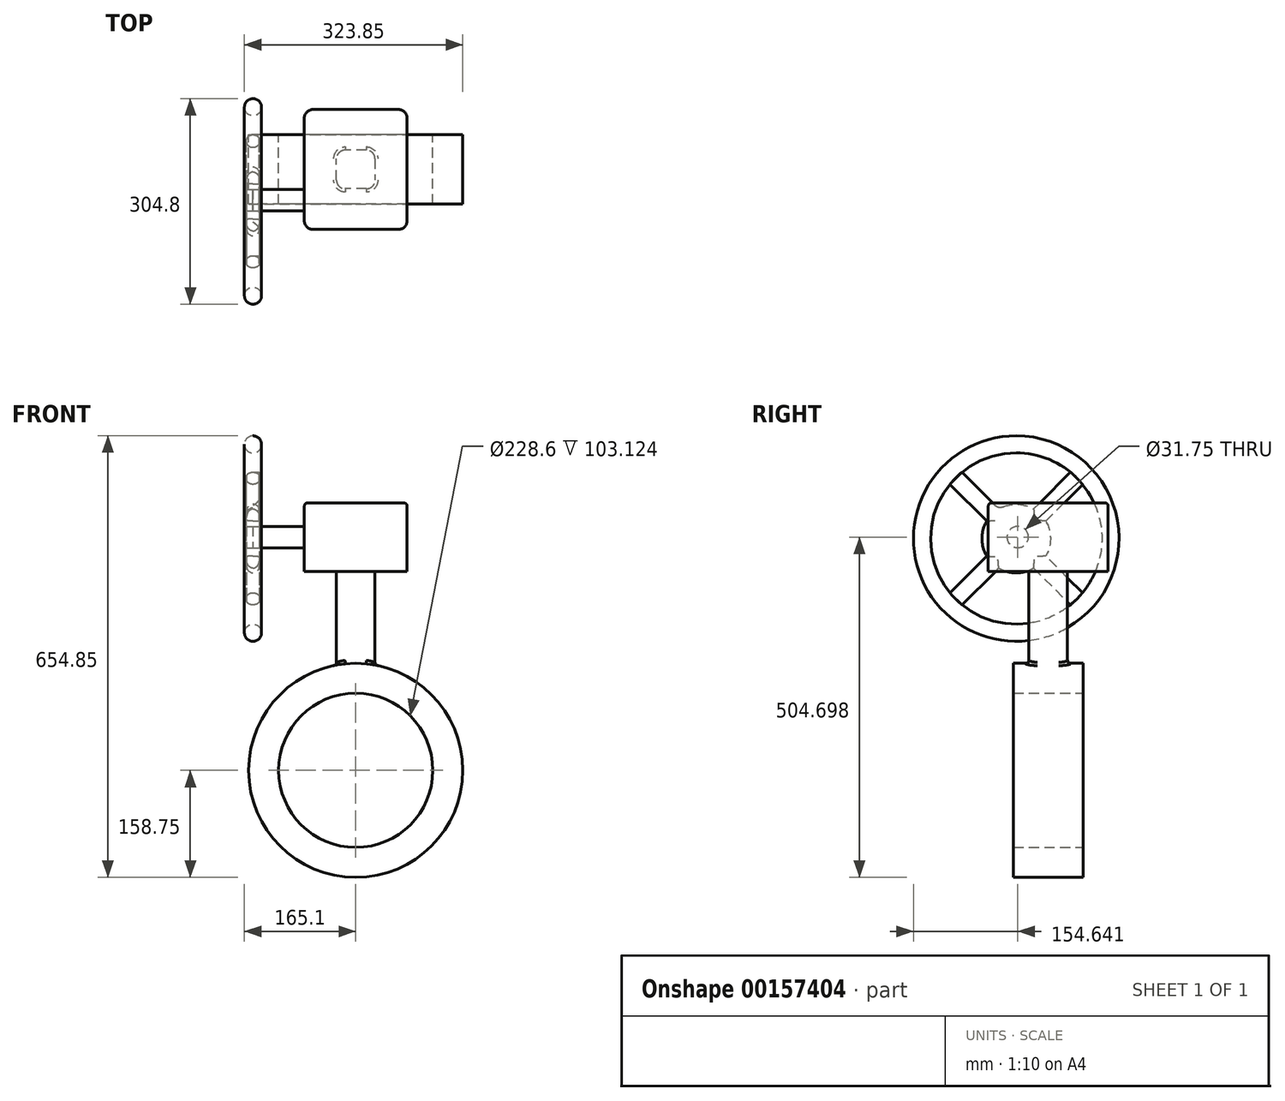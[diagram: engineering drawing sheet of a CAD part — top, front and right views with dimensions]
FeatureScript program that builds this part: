
annotation { "Feature Type Name" : "Feature", "Feature Type Description" : "" }
export const myFeature = defineFeature(function(context is Context, id is Id, definition is map)
    precondition{}
    {
        {
            var Q0;
            Q0=qCreatedBy(makeId("Front.planeOp"),FACE);
            var sketch = newSketch(context, id + "F0", { "sketchPlane" : qUnion([Q0])});
            skCircle(sketch, "E0", {"center": v(0, 0) * mm, "radius": 158.75 * mm});
            skSolve(sketch);
        }
        {
            var Q0;
            Q0=makeQuery(id+"F0.imprint","IMPRINT",FACE,{"disambiguationData":[TD([[makeQuery(id+"F0.imprint","IMPRINT",EDGE,{"derivedFrom":sQuery(id+"F0.wireOp",EDGE,"E0")}),1.0]])]});
            extrude(context, id + "F1", {"entities" : qUnion([Q0]), "depth" : 103.12 * mm, "symmetric" : true});
        }
        {
            var Q0;
            Q0=qCreatedBy(makeId("Top.planeOp"),FACE);
            cPlane(context, id + "F2", {"entities" : qUnion([Q0]), "cplaneType" : CPlaneType.OFFSET, "offset" : 152.4 * mm, "width" : 152.4 * mm, "height" : 152.4 * mm});
        }
        {
            var Q0;
            Q0=qCreatedBy(id+"F2.planeOp",FACE);
            var sketch = newSketch(context, id + "F3", { "sketchPlane" : qUnion([Q0])});
            skLineSegment(sketch, "E1.bottom", {"start": v(28.57, -28.58) * mm, "end": v(-28.58, -28.58) * mm});
            skLineSegment(sketch, "E1.top", {"start": v(28.57, 28.58) * mm, "end": v(-28.58, 28.57) * mm});
            skLineSegment(sketch, "E1.left", {"start": v(28.57, -28.57) * mm, "end": v(28.57, 28.58) * mm});
            skLineSegment(sketch, "E1.right", {"start": v(-28.58, -28.58) * mm, "end": v(-28.58, 28.57) * mm});
            skPoint(sketch, "E1.middle", {"position": v(0, 0) * mm});
            skSolve(sketch);
        }
        {
            var Q0;
            Q0 = qSketchRegion(id + "F3", true);
            extrude(context, id + "F4", {"entities" : qUnion([Q0]), "operationType" : NewBodyOperationType.ADD, "depth" : 142.75 * mm});
        }
        {
            var Q0;
            Q0=makeQuery(id+"F4.opExtrude","CAP_FACE",FACE,{"disambiguationData":[OSD([sQuery(id+"F3.wireOp",EDGE,"E1.bottom"),sQuery(id+"F3.wireOp",EDGE,"E1.top"),sQuery(id+"F3.wireOp",EDGE,"E1.left"),sQuery(id+"F3.wireOp",EDGE,"E1.right")])],"isStart":false});
            var sketch = newSketch(context, id + "F5", { "sketchPlane" : qUnion([Q0])});
            skLineSegment(sketch, "E2.bottom", {"start": v(76.2, -88.9) * mm, "end": v(-76.2, -88.9) * mm});
            skLineSegment(sketch, "E2.top", {"start": v(76.2, 88.9) * mm, "end": v(-76.2, 88.9) * mm});
            skLineSegment(sketch, "E2.left", {"start": v(76.2, -88.9) * mm, "end": v(76.2, 88.9) * mm});
            skLineSegment(sketch, "E2.right", {"start": v(-76.2, -88.9) * mm, "end": v(-76.2, 88.9) * mm});
            skPoint(sketch, "E2.middle", {"position": v(0, 0) * mm});
            skSolve(sketch);
        }
        {
            var Q0;
            Q0 = qSketchRegion(id + "F5", true);
            extrude(context, id + "F6", {"entities" : qUnion([Q0]), "operationType" : NewBodyOperationType.ADD, "depth" : 101.6 * mm});
        }
        {
            var Q0;
            Q0=makeQuery(id+"F6.opExtrude","SWEPT_FACE",FACE,{"disambiguationData":[OSD([sQuery(id+"F5.wireOp",EDGE,"E2.right")])]});
            var sketch = newSketch(context, id + "F7", { "sketchPlane" : qUnion([Q0])});
            skCircle(sketch, "E3", {"center": v(45.22, 345.95) * mm, "radius": 15.88 * mm});
            skPoint(sketch, "E3.centerSnap0", {"position": v(88.9, 345.95) * mm});
            skSolve(sketch);
        }
        {
            var Q0;
            Q0 = qSketchRegion(id + "F7", true);
            extrude(context, id + "F8", {"entities" : qUnion([Q0]), "operationType" : NewBodyOperationType.ADD, "depth" : 76.2 * mm});
        }
        {
            var Q0;
            Q0=makeQuery(id+"F8.opExtrude","CAP_FACE",FACE,{"disambiguationData":[OSD([sQuery(id+"F7.wireOp",EDGE,"E3")])],"isStart":false});
            var sketch = newSketch(context, id + "F9", { "sketchPlane" : qUnion([Q0])});
            skCircle(sketch, "E4", {"center": v(47.46, 343.7) * mm, "radius": 152.4 * mm});
            skArc(sketch, "E5", {"start": v(73.26, 387.46) * mm, "mid": v(47.46, 394.5) * mm, "end": v(21.66, 387.46) * mm});
            skCircle(sketch, "E6", {"center": v(47.46, 343.7) * mm, "radius": 127 * mm});
            skLineSegment(sketch, "E7.trimOffspring", {"start": v(91.22, 317.9) * mm, "end": v(145.8, 263.33) * mm});
            skLineSegment(sketch, "E8.trimOffspring", {"start": v(73.26, 299.94) * mm, "end": v(127.84, 245.37) * mm});
            skLineSegment(sketch, "E9.trimOffspring", {"start": v(21.66, 299.94) * mm, "end": v(-32.9, 245.37) * mm});
            skLineSegment(sketch, "E10.trimOffspring", {"start": v(3.7, 317.9) * mm, "end": v(-50.87, 263.33) * mm});
            skLineSegment(sketch, "E11.trimOffspring", {"start": v(3.7, 369.5) * mm, "end": v(-50.87, 424.08) * mm});
            skLineSegment(sketch, "E12.trimOffspring", {"start": v(21.66, 387.46) * mm, "end": v(-32.9, 442.04) * mm});
            skLineSegment(sketch, "E13.trimOffspring", {"start": v(73.26, 387.46) * mm, "end": v(127.84, 442.04) * mm});
            skLineSegment(sketch, "E14.trimOffspring", {"start": v(91.22, 369.5) * mm, "end": v(145.8, 424.08) * mm});
            skArc(sketch, "E15.trimOffspring", {"start": v(91.22, 317.9) * mm, "mid": v(98.26, 343.7) * mm, "end": v(91.22, 369.5) * mm});
            skArc(sketch, "E16.trimOffspring", {"start": v(21.66, 299.94) * mm, "mid": v(47.46, 292.9) * mm, "end": v(73.26, 299.94) * mm});
            skArc(sketch, "E17.trimOffspring", {"start": v(3.7, 369.5) * mm, "mid": v(-3.34, 343.7) * mm, "end": v(3.7, 317.9) * mm});
            skSolve(sketch);
        }
        {
            var Q0;
            Q0 = qSketchRegion(id + "F9", true);
            extrude(context, id + "F10", {"entities" : qUnion([Q0]), "depth" : 25.4 * mm, "symmetric" : true});
        }
        {
            var Q0;
            Q0=makeQuery(id+"F9.imprint","IMPRINT",FACE,{"disambiguationData":[TD([[makeQuery(id+"F9.imprint","IMPRINT",EDGE,{"derivedFrom":sQuery(id+"F9.wireOp",EDGE,"E5")}),1.0]])]});
            extrude(context, id + "F11", {"entities" : qUnion([Q0]), "depth" : 19.05 * mm, "symmetric" : true});
        }
        {
            var Q0;
            Q0=makeQuery(id+"F10.opExtrude","CAP_EDGE",EDGE,{"disambiguationData":[OSD([sQuery(id+"F9.wireOp",EDGE,"E6")])],"isStart":false});
            var Q1;
            Q1=makeQuery(id+"F10.opExtrude","CAP_EDGE",EDGE,{"disambiguationData":[OSD([sQuery(id+"F9.wireOp",EDGE,"E4")])],"isStart":false});
            var Q2;
            Q2=makeQuery(id+"F10.opExtrude","CAP_EDGE",EDGE,{"disambiguationData":[OSD([sQuery(id+"F9.wireOp",EDGE,"E4")])],"isStart":true});
            var Q3;
            Q3=makeQuery(id+"F10.opExtrude","CAP_EDGE",EDGE,{"disambiguationData":[OSD([sQuery(id+"F9.wireOp",EDGE,"E6")])],"isStart":true});
            fillet(context, id + "F12", {"entities" : qUnion([Q0, Q1, Q2, Q3]), "radius" : 12.7 * mm, "tangentPropagation" : true, "allowEdgeOverflow" : false});
        }
        {
            var Q0;
            Q0=makeQuery(id+"F11.opExtrude","CAP_EDGE",EDGE,{"disambiguationData":[OSD([sQuery(id+"F9.wireOp",EDGE,"E12.trimOffspring")])],"isStart":false});
            var Q1;
            Q1=makeQuery(id+"F11.opExtrude","CAP_EDGE",EDGE,{"disambiguationData":[OSD([sQuery(id+"F9.wireOp",EDGE,"E5")])],"isStart":false});
            var Q2;
            Q2=makeQuery(id+"F11.opExtrude","CAP_EDGE",EDGE,{"disambiguationData":[OSD([sQuery(id+"F9.wireOp",EDGE,"E13.trimOffspring")])],"isStart":false});
            var Q3;
            Q3=makeQuery(id+"F11.opExtrude","CAP_EDGE",EDGE,{"disambiguationData":[OSD([sQuery(id+"F9.wireOp",EDGE,"E11.trimOffspring")])],"isStart":false});
            var Q4;
            Q4=makeQuery(id+"F11.opExtrude","CAP_EDGE",EDGE,{"disambiguationData":[OSD([sQuery(id+"F9.wireOp",EDGE,"E17.trimOffspring")])],"isStart":false});
            var Q5;
            Q5=makeQuery(id+"F11.opExtrude","CAP_EDGE",EDGE,{"disambiguationData":[OSD([sQuery(id+"F9.wireOp",EDGE,"E10.trimOffspring")])],"isStart":false});
            var Q6;
            Q6=makeQuery(id+"F11.opExtrude","CAP_EDGE",EDGE,{"disambiguationData":[OSD([sQuery(id+"F9.wireOp",EDGE,"E14.trimOffspring")])],"isStart":false});
            var Q7;
            Q7=makeQuery(id+"F11.opExtrude","CAP_EDGE",EDGE,{"disambiguationData":[OSD([sQuery(id+"F9.wireOp",EDGE,"E15.trimOffspring")])],"isStart":false});
            var Q8;
            Q8=makeQuery(id+"F11.opExtrude","CAP_EDGE",EDGE,{"disambiguationData":[OSD([sQuery(id+"F9.wireOp",EDGE,"E7.trimOffspring")])],"isStart":false});
            var Q9;
            Q9=makeQuery(id+"F11.opExtrude","CAP_EDGE",EDGE,{"disambiguationData":[OSD([sQuery(id+"F9.wireOp",EDGE,"E8.trimOffspring")])],"isStart":false});
            var Q10;
            Q10=makeQuery(id+"F11.opExtrude","CAP_EDGE",EDGE,{"disambiguationData":[OSD([sQuery(id+"F9.wireOp",EDGE,"E16.trimOffspring")])],"isStart":false});
            var Q11;
            Q11=makeQuery(id+"F11.opExtrude","CAP_EDGE",EDGE,{"disambiguationData":[OSD([sQuery(id+"F9.wireOp",EDGE,"E9.trimOffspring")])],"isStart":false});
            var Q12;
            Q12=makeQuery(id+"F11.opExtrude","CAP_EDGE",EDGE,{"disambiguationData":[OSD([sQuery(id+"F9.wireOp",EDGE,"E14.trimOffspring")])],"isStart":true});
            var Q13;
            Q13=makeQuery(id+"F11.opExtrude","SWEPT_EDGE",EDGE,{"disambiguationData":[OSD([sQuery(id+"F9.wireOp",EDGE,"E5"),sQuery(id+"F9.wireOp",EDGE,"E13.trimOffspring")])]});
            var Q14;
            Q14=makeQuery(id+"F11.opExtrude","CAP_EDGE",EDGE,{"disambiguationData":[OSD([sQuery(id+"F9.wireOp",EDGE,"E11.trimOffspring")])],"isStart":true});
            var Q15;
            Q15=makeQuery(id+"F11.opExtrude","CAP_EDGE",EDGE,{"disambiguationData":[OSD([sQuery(id+"F9.wireOp",EDGE,"E12.trimOffspring")])],"isStart":true});
            var Q16;
            Q16=makeQuery(id+"F11.opExtrude","CAP_EDGE",EDGE,{"disambiguationData":[OSD([sQuery(id+"F9.wireOp",EDGE,"E5")])],"isStart":true});
            var Q17;
            Q17=makeQuery(id+"F11.opExtrude","CAP_EDGE",EDGE,{"disambiguationData":[OSD([sQuery(id+"F9.wireOp",EDGE,"E15.trimOffspring")])],"isStart":true});
            var Q18;
            Q18=makeQuery(id+"F11.opExtrude","CAP_EDGE",EDGE,{"disambiguationData":[OSD([sQuery(id+"F9.wireOp",EDGE,"E7.trimOffspring")])],"isStart":true});
            var Q19;
            Q19=makeQuery(id+"F11.opExtrude","CAP_EDGE",EDGE,{"disambiguationData":[OSD([sQuery(id+"F9.wireOp",EDGE,"E8.trimOffspring")])],"isStart":true});
            var Q20;
            Q20=makeQuery(id+"F11.opExtrude","CAP_EDGE",EDGE,{"disambiguationData":[OSD([sQuery(id+"F9.wireOp",EDGE,"E16.trimOffspring")])],"isStart":true});
            var Q21;
            Q21=makeQuery(id+"F11.opExtrude","CAP_EDGE",EDGE,{"disambiguationData":[OSD([sQuery(id+"F9.wireOp",EDGE,"E17.trimOffspring")])],"isStart":true});
            var Q22;
            Q22=makeQuery(id+"F11.opExtrude","CAP_EDGE",EDGE,{"disambiguationData":[OSD([sQuery(id+"F9.wireOp",EDGE,"E10.trimOffspring")])],"isStart":true});
            var Q23;
            Q23=makeQuery(id+"F11.opExtrude","CAP_EDGE",EDGE,{"disambiguationData":[OSD([sQuery(id+"F9.wireOp",EDGE,"E9.trimOffspring")])],"isStart":true});
            fillet(context, id + "F13", {"entities" : qUnion([Q0, Q1, Q2, Q3, Q4, Q5, Q6, Q7, Q8, Q9, Q10, Q11, Q12, Q13, Q14, Q15, Q16, Q17, Q18, Q19, Q20, Q21, Q22, Q23]), "radius" : 9.52 * mm, "tangentPropagation" : true, "allowEdgeOverflow" : false});
        }
        {
            var Q0;
            Q0=makeQuery(id+"F1.opExtrude","CAP_FACE",FACE,{"disambiguationData":[OSD([sQuery(id+"F0.wireOp",EDGE,"E0")])],"isStart":true});
            var sketch = newSketch(context, id + "F14", { "sketchPlane" : qUnion([Q0])});
            skCircle(sketch, "E18", {"center": v(0, 0) * mm, "radius": 114.3 * mm});
            skSolve(sketch);
        }
        {
            var Q0;
            Q0 = qSketchRegion(id + "F14", true);
            extrude(context, id + "F15", {"entities" : qUnion([Q0]), "operationType" : NewBodyOperationType.REMOVE, "endBound" : BoundingType.THROUGH_ALL, "oppositeDirection" : true, "depth" : 25.4 * mm});
        }
        {
            var Q0;
            Q0=makeQuery(id+"F4.opExtrude","SWEPT_EDGE",EDGE,{"disambiguationData":[OSD([sQuery(id+"F3.wireOp",EDGE,"E1.top"),sQuery(id+"F3.wireOp",EDGE,"E1.left")])]});
            var Q1;
            Q1=makeQuery(id+"F4.opExtrude","SWEPT_EDGE",EDGE,{"disambiguationData":[OSD([sQuery(id+"F3.wireOp",EDGE,"E1.top"),sQuery(id+"F3.wireOp",EDGE,"E1.right")])]});
            var Q2;
            Q2=makeQuery(id+"F4.opExtrude","SWEPT_EDGE",EDGE,{"disambiguationData":[OSD([sQuery(id+"F3.wireOp",EDGE,"E1.bottom"),sQuery(id+"F3.wireOp",EDGE,"E1.left")])]});
            var Q3;
            Q3=makeQuery(id+"F4.opExtrude","SWEPT_EDGE",EDGE,{"disambiguationData":[OSD([sQuery(id+"F3.wireOp",EDGE,"E1.bottom"),sQuery(id+"F3.wireOp",EDGE,"E1.right")])]});
            var Q4;
            Q4=makeQuery(id+"F6.opExtrude","SWEPT_EDGE",EDGE,{"disambiguationData":[OSD([sQuery(id+"F5.wireOp",EDGE,"E2.bottom"),sQuery(id+"F5.wireOp",EDGE,"E2.right")])]});
            var Q5;
            Q5=makeQuery(id+"F6.opExtrude","SWEPT_EDGE",EDGE,{"disambiguationData":[OSD([sQuery(id+"F5.wireOp",EDGE,"E2.bottom"),sQuery(id+"F5.wireOp",EDGE,"E2.left")])]});
            var Q6;
            Q6=makeQuery(id+"F6.opExtrude","SWEPT_EDGE",EDGE,{"disambiguationData":[OSD([sQuery(id+"F5.wireOp",EDGE,"E2.top"),sQuery(id+"F5.wireOp",EDGE,"E2.right")])]});
            var Q7;
            Q7=makeQuery(id+"F6.opExtrude","SWEPT_EDGE",EDGE,{"disambiguationData":[OSD([sQuery(id+"F5.wireOp",EDGE,"E2.top"),sQuery(id+"F5.wireOp",EDGE,"E2.left")])]});
            fillet(context, id + "F16", {"entities" : qUnion([Q0, Q1, Q2, Q3, Q4, Q5, Q6, Q7]), "radius" : 12.7 * mm, "tangentPropagation" : true, "allowEdgeOverflow" : false});
        }
        {
            var Q0;
            Q0=makeQuery(id+"F6.opExtrude","CAP_EDGE",EDGE,{"disambiguationData":[OSD([sQuery(id+"F5.wireOp",EDGE,"E2.top")])],"isStart":false});
            fillet(context, id + "F17", {"entities" : qUnion([Q0]), "radius" : 5.08 * mm, "tangentPropagation" : true, "allowEdgeOverflow" : false});
        }
        {
            var Q0;
            Q0=makeQuery(id+"F4.boolean.opBoolean","INTERSECT",EDGE,{"derivedFrom":[makeQuery(id+"F1.opExtrude","SWEPT_FACE",FACE,{"disambiguationData":[OSD([sQuery(id+"F0.wireOp",EDGE,"E0")])]}),makeQuery(id+"F4.opExtrude","SWEPT_FACE",FACE,{"disambiguationData":[OSD([sQuery(id+"F3.wireOp",EDGE,"E1.bottom")])]})]});
            fillet(context, id + "F18", {"entities" : qUnion([Q0]), "radius" : 5.08 * mm, "tangentPropagation" : true, "allowEdgeOverflow" : false});
        }
    });
